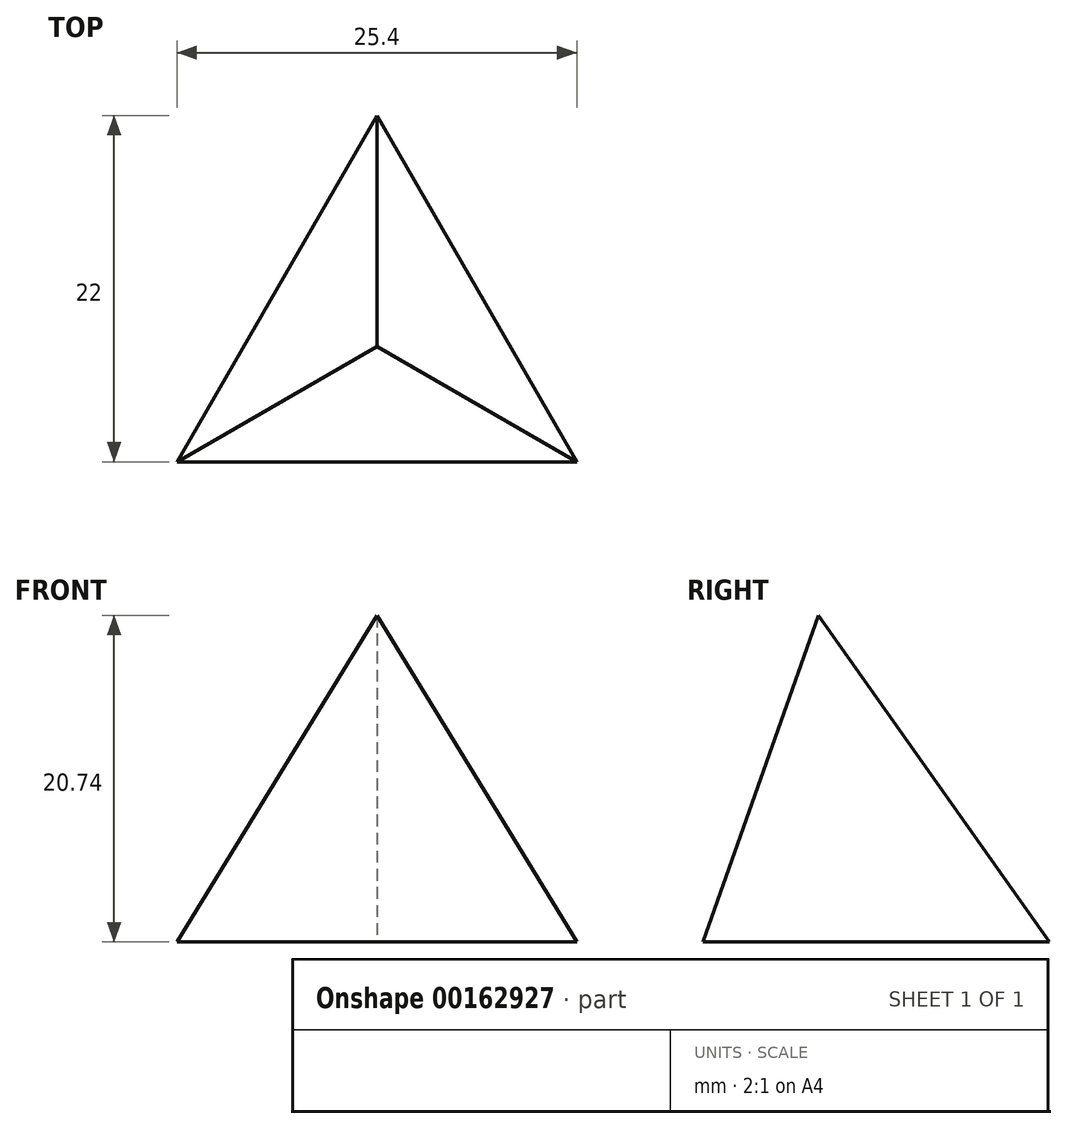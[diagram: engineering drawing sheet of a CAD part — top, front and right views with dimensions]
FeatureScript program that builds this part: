
annotation { "Feature Type Name" : "Feature", "Feature Type Description" : "" }
export const myFeature = defineFeature(function(context is Context, id is Id, definition is map)
    precondition{}
    {
        {
            var Q0;
            Q0=qCreatedBy(makeId("Top.planeOp"),FACE);
            var sketch = newSketch(context, id + "F0", { "sketchPlane" : qUnion([Q0])});
            skLineSegment(sketch, "E0", {"start": v(-12.7, 0) * mm, "end": v(0, 22) * mm});
            skLineSegment(sketch, "E1", {"start": v(0, 22) * mm, "end": v(12.7, 0) * mm});
            skLineSegment(sketch, "E2", {"start": v(12.7, 0) * mm, "end": v(-12.7, 0) * mm});
            skSolve(sketch);
        }
        {
            var Q0;
            Q0=makeQuery(id+"F0.imprint","IMPRINT",FACE,{"disambiguationData":[TD([[makeQuery(id+"F0.imprint","IMPRINT",EDGE,{"derivedFrom":sQuery(id+"F0.wireOp",EDGE,"E0")}),-1.0]])]});
            extrude(context, id + "F1", {"entities" : qUnion([Q0]), "depth" : 25.4 * mm, "hasDraft" : true, "draftAngle" : 90 * degree - atan(2 * (2 ^ 0.5)), "draftPullDirection" : true});
        }
    });
